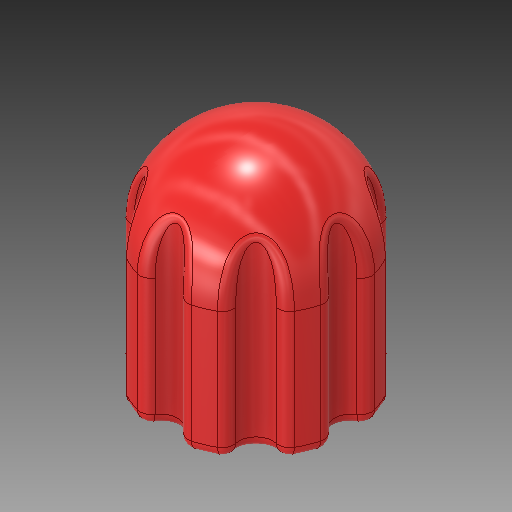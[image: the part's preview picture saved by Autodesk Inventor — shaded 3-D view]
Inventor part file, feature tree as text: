
AUTODESK INVENTOR PART (.ipt)
format: ipt  version: 2018 (Build 220112000, 112)  size: 461,312 bytes
history: native  units: mm
features: sketch x2, revolve x1, extrude x1, fillet x1
ambient origin geometry x8: Origin, YZ Plane, XZ Plane, XY Plane, X Axis, Y Axis, Z Axis, Center Point
bodies: Solid1 (feature_tree)
feature tree (5):
  revolve  "Revolution1"  [1 undecoded]
  extrude  "Extrusion1"  Depth=2.0mm
  fillet  "Fillet1"  Radius=2.0mm
  sketch  "Sketch1"  dims[d0=5.0mm d1=17.0mm]
  sketch  "Sketch2"  dims[d2=21.13mm d3=23.0mm d4=2.0mm d5=1.0mm d6=90.0deg d7=17.0mm d8=6.0mm d9=80.0mm d11=360.0deg d13=10.0mm d14=0.0mm d15=2.0mm]
note: 1 required parameter value undecoded (feature->parameter linkage not recoverable at this tier; creation-order binding heuristic only, values carry confidence <= 0.55)
